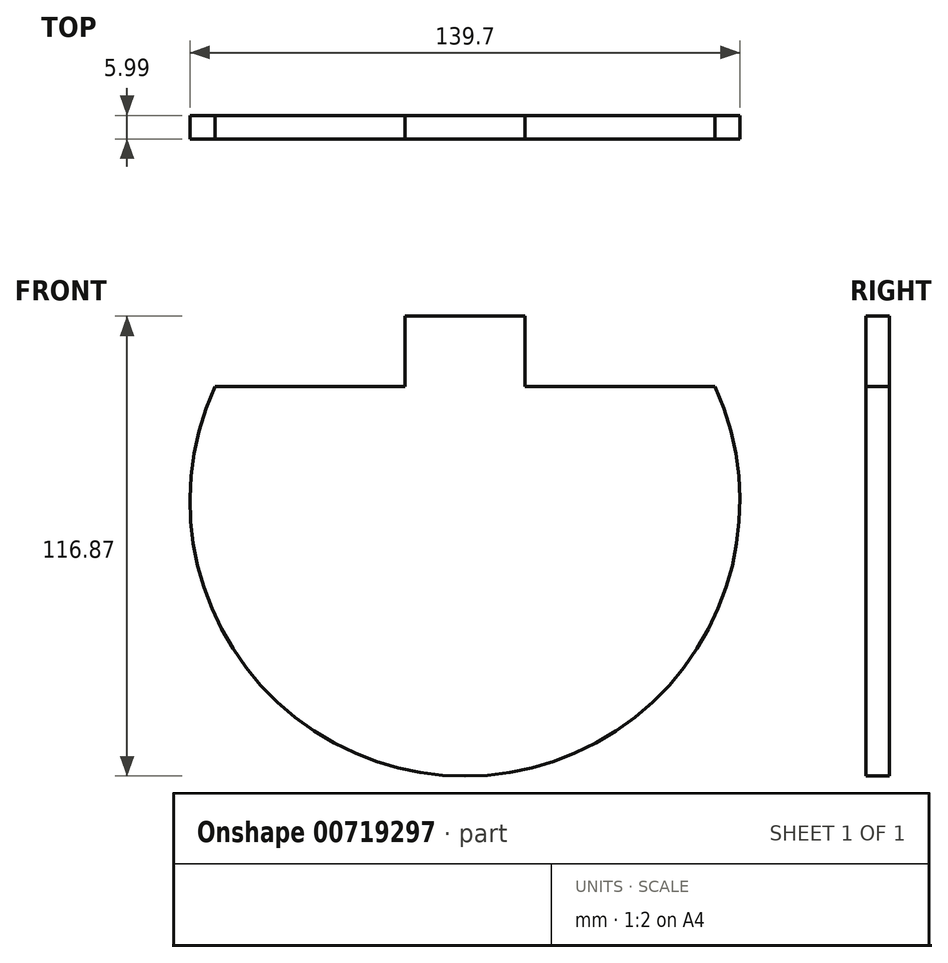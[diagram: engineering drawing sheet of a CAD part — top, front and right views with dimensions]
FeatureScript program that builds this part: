
annotation { "Feature Type Name" : "Feature", "Feature Type Description" : "" }
export const myFeature = defineFeature(function(context is Context, id is Id, definition is map)
    precondition{}
    {
        {
            var Q0;
            Q0=qCreatedBy(makeId("Front.planeOp"),FACE);
            var sketch = newSketch(context, id + "F0", { "sketchPlane" : qUnion([Q0])});
            skArc(sketch, "E0", {"start": v(-63.5, 29.1) * mm, "mid": v(0, -69.85) * mm, "end": v(63.5, 29.1) * mm});
            skLineSegment(sketch, "E1", {"start": v(0, 0) * mm, "end": v(0, 47.02) * mm, "construction": true});
            skLineSegment(sketch, "E2", {"start": v(-63.5, 29.1) * mm, "end": v(-15.24, 29.1) * mm});
            skLineSegment(sketch, "E3", {"start": v(63.5, 29.1) * mm, "end": v(15.24, 29.1) * mm});
            skLineSegment(sketch, "E4", {"start": v(-15.24, 29.1) * mm, "end": v(-15.24, 47.02) * mm});
            skLineSegment(sketch, "E5", {"start": v(-15.24, 47.02) * mm, "end": v(15.24, 47.02) * mm});
            skLineSegment(sketch, "E6", {"start": v(15.24, 29.1) * mm, "end": v(15.24, 47.02) * mm});
            skSolve(sketch);
        }
        {
            var Q0;
            Q0=makeQuery(id+"F0.imprint","IMPRINT",FACE,{"disambiguationData":[TD([[makeQuery(id+"F0.imprint","IMPRINT",EDGE,{"derivedFrom":sQuery(id+"F0.wireOp",EDGE,"E0")}),1.0]])]});
            extrude(context, id + "F1", {"entities" : qUnion([Q0]), "depth" : 6 * mm, "offsetDistance" : 25.4 * mm});
        }
    });
